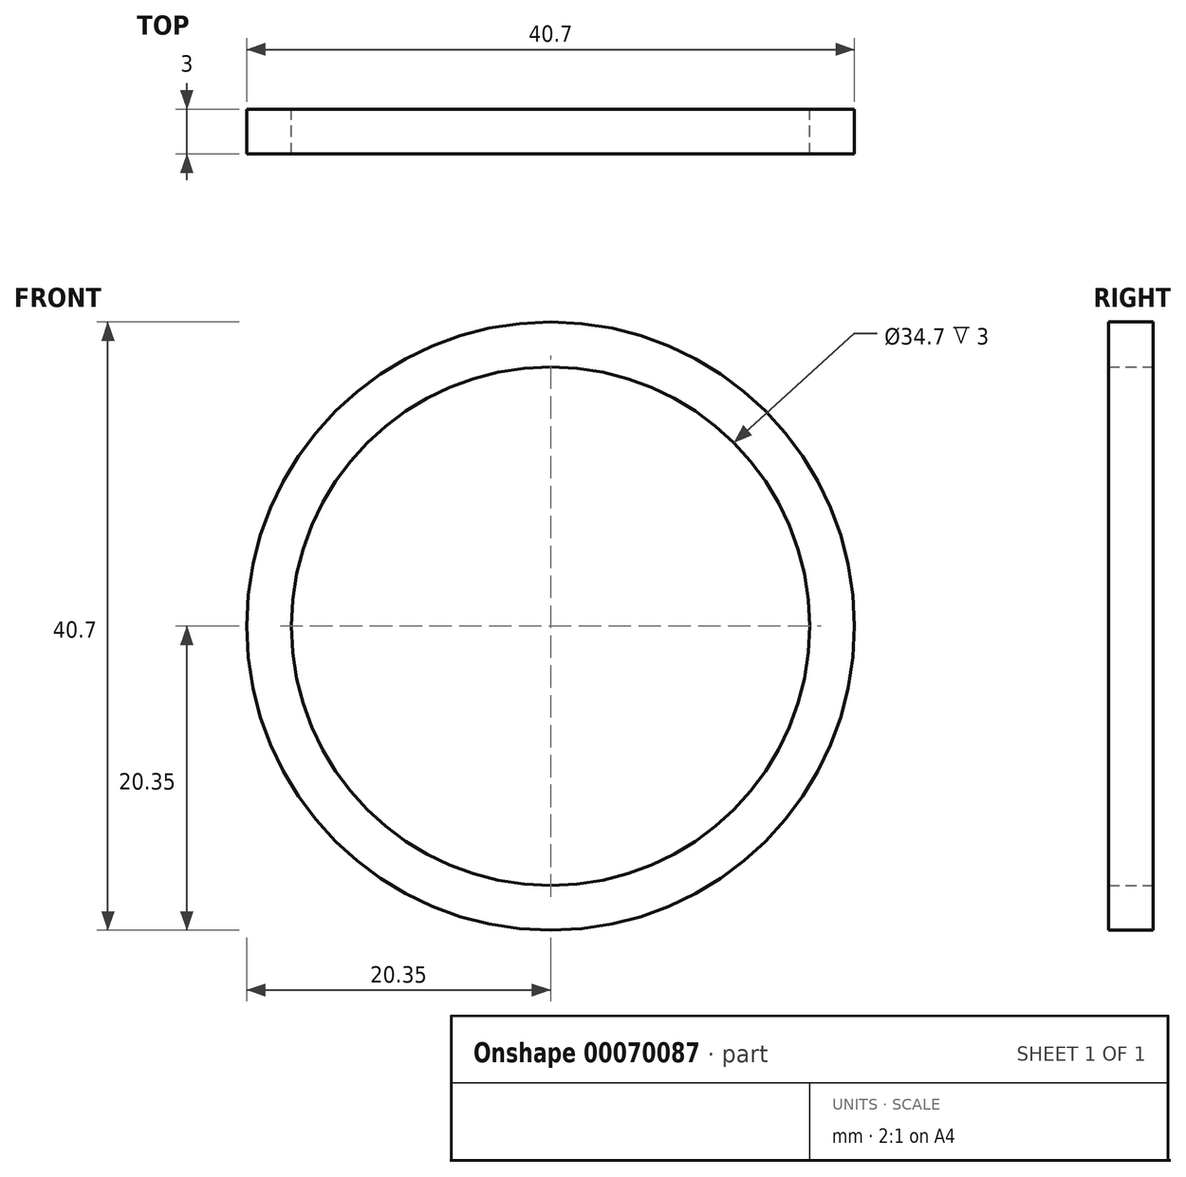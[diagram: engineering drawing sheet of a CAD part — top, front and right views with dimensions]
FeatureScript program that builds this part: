
annotation { "Feature Type Name" : "Feature", "Feature Type Description" : "" }
export const myFeature = defineFeature(function(context is Context, id is Id, definition is map)
    precondition{}
    {
        {
            var Q0;
            Q0=qCreatedBy(makeId("Front.planeOp"),FACE);
            var sketch = newSketch(context, id + "F0", { "sketchPlane" : qUnion([Q0])});
            skCircle(sketch, "E0", {"center": v(0, 0) * mm, "radius": 17.35 * mm});
            skCircle(sketch, "E1", {"center": v(0, 0) * mm, "radius": 20.35 * mm});
            skSolve(sketch);
        }
        {
            var Q0;
            Q0 = qSketchRegion(id + "F0", true);
            extrude(context, id + "F1", {"entities" : qUnion([Q0]), "depth" : 3 * mm});
        }
    });
